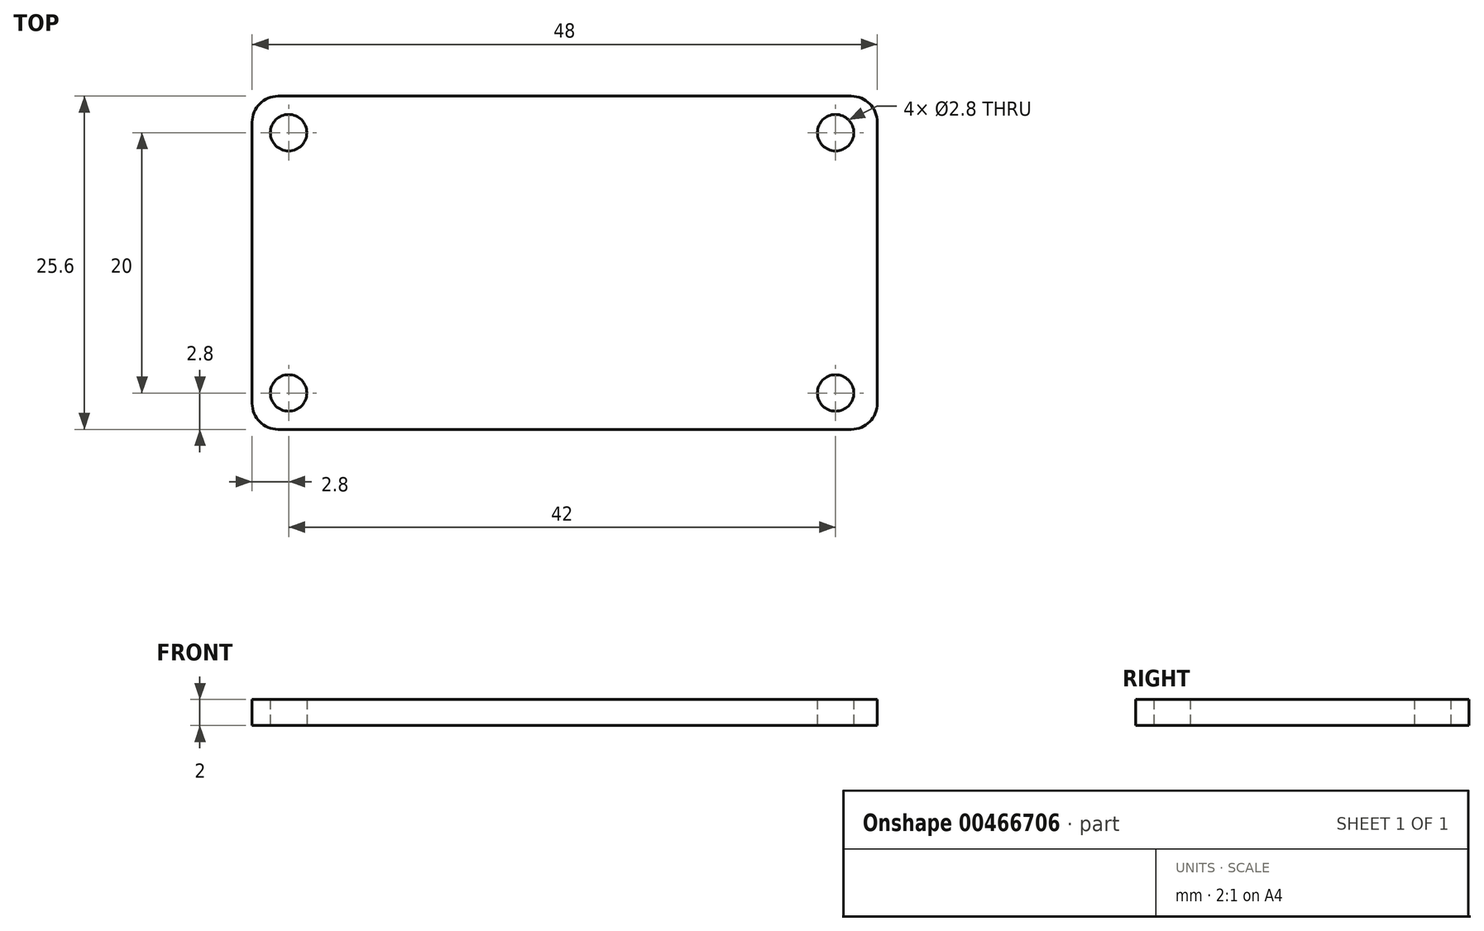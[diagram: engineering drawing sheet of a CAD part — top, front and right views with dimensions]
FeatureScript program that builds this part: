
annotation { "Feature Type Name" : "Feature", "Feature Type Description" : "" }
export const myFeature = defineFeature(function(context is Context, id is Id, definition is map)
    precondition{}
    {
        {
            var Q0;
            Q0=qCreatedBy(makeId("Top.planeOp"),FACE);
            var sketch = newSketch(context, id + "F0", { "sketchPlane" : qUnion([Q0])});
            skLineSegment(sketch, "E0.bottom", {"start": v(-22, 12.8) * mm, "end": v(22, 12.8) * mm});
            skLineSegment(sketch, "E0.top", {"start": v(-22, -12.8) * mm, "end": v(22, -12.8) * mm});
            skLineSegment(sketch, "E0.left", {"start": v(-24, 10.8) * mm, "end": v(-24, -10.8) * mm});
            skLineSegment(sketch, "E0.right", {"start": v(24, 10.8) * mm, "end": v(24, -10.8) * mm});
            skPoint(sketch, "E0.middle", {"position": v(0, 0) * mm});
            skCircle(sketch, "E1", {"center": v(-21.2, 10) * mm, "radius": 1.4 * mm});
            skCircle(sketch, "E2", {"center": v(20.8, 10) * mm, "radius": 1.4 * mm});
            skCircle(sketch, "E3.MirrorC", {"center": v(-21.2, -10) * mm, "radius": 1.4 * mm});
            skCircle(sketch, "E4.MirrorC", {"center": v(20.8, -10) * mm, "radius": 1.4 * mm});
            skPoint(sketch, "E5.visualSharp", {"position": v(24, 12.8) * mm});
            skArc(sketch, "E5.filletArc", {"start": v(24, 10.8) * mm, "mid": v(23.41, 12.21) * mm, "end": v(22, 12.8) * mm});
            skPoint(sketch, "E6.visualSharp", {"position": v(24, -12.8) * mm});
            skArc(sketch, "E6.filletArc", {"start": v(22, -12.8) * mm, "mid": v(23.41, -12.21) * mm, "end": v(24, -10.8) * mm});
            skPoint(sketch, "E7.visualSharp", {"position": v(-24, -12.8) * mm});
            skArc(sketch, "E7.filletArc", {"start": v(-24, -10.8) * mm, "mid": v(-23.41, -12.21) * mm, "end": v(-22, -12.8) * mm});
            skPoint(sketch, "E8.visualSharp", {"position": v(-24, 12.8) * mm});
            skArc(sketch, "E8.filletArc", {"start": v(-22, 12.8) * mm, "mid": v(-23.41, 12.21) * mm, "end": v(-24, 10.8) * mm});
            skSolve(sketch);
        }
        {
            var Q0;
            Q0=makeQuery(id+"F0.imprint","IMPRINT",FACE,{"disambiguationData":[TD([[makeQuery(id+"F0.imprint","IMPRINT",EDGE,{"derivedFrom":sQuery(id+"F0.wireOp",EDGE,"E0.bottom")}),-1.0]])]});
            extrude(context, id + "F1", {"entities" : qUnion([Q0]), "depth" : 2 * mm, "offsetDistance" : 25 * mm});
        }
    });
